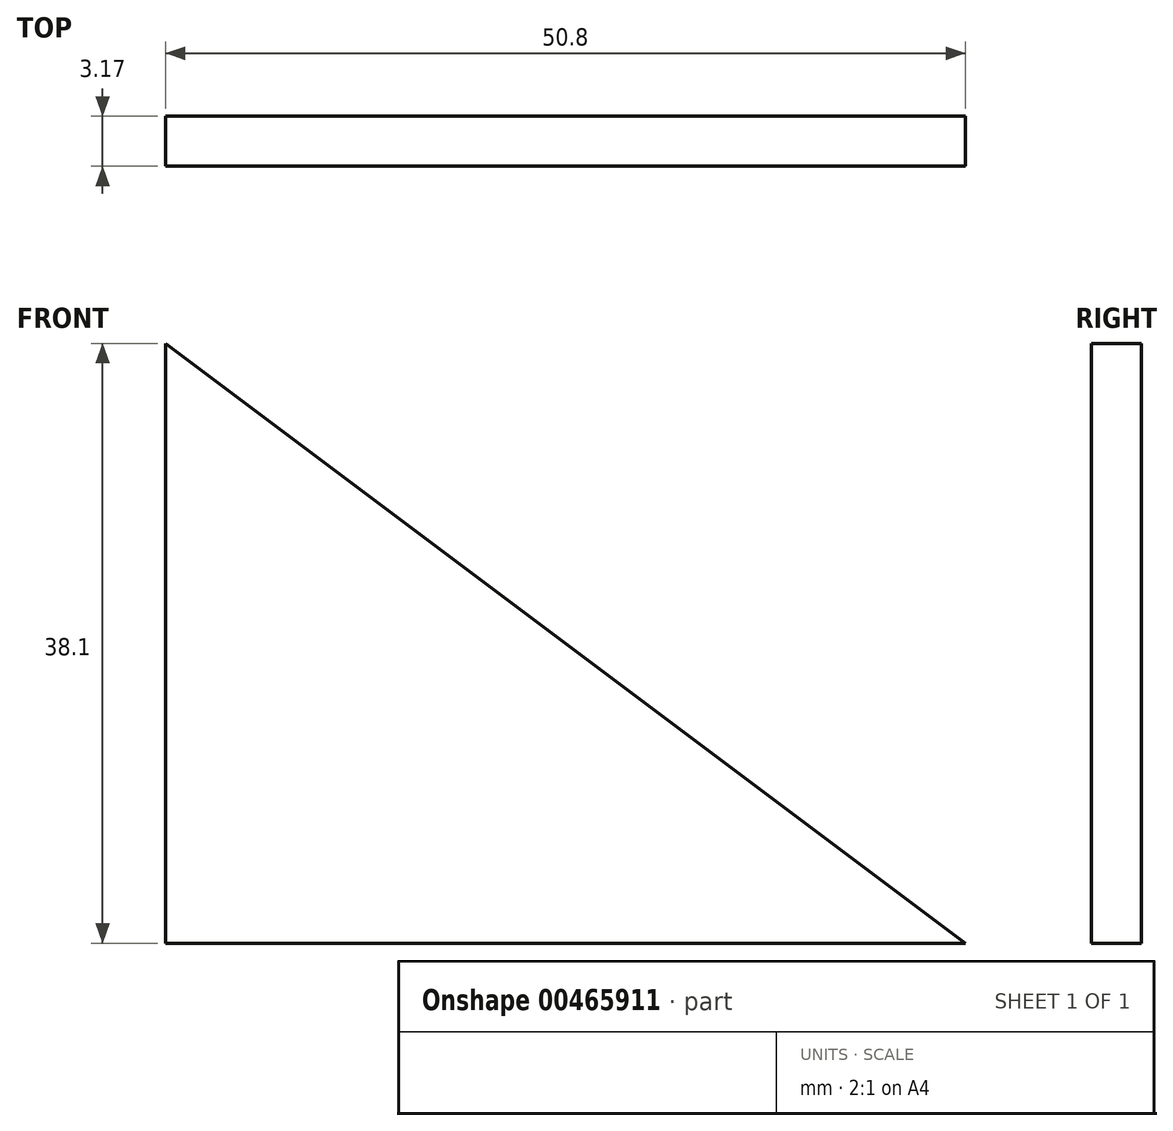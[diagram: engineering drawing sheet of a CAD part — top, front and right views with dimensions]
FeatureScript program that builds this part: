
annotation { "Feature Type Name" : "Feature", "Feature Type Description" : "" }
export const myFeature = defineFeature(function(context is Context, id is Id, definition is map)
    precondition{}
    {
        {
            var Q0;
            Q0=qCreatedBy(makeId("Front.planeOp"),FACE);
            var sketch = newSketch(context, id + "F0", { "sketchPlane" : qUnion([Q0])});
            skLineSegment(sketch, "E0.bottom", {"start": v(-25.4, 19.05) * mm, "end": v(25.4, 19.05) * mm});
            skLineSegment(sketch, "E0.top", {"start": v(-25.4, -19.05) * mm, "end": v(25.4, -19.05) * mm});
            skLineSegment(sketch, "E0.left", {"start": v(-25.4, 19.05) * mm, "end": v(-25.4, -19.05) * mm});
            skLineSegment(sketch, "E0.right", {"start": v(25.4, 19.05) * mm, "end": v(25.4, -19.05) * mm});
            skPoint(sketch, "E0.middle", {"position": v(0, 0) * mm});
            skLineSegment(sketch, "E1", {"start": v(-25.4, 19.05) * mm, "end": v(25.4, -19.05) * mm});
            skSolve(sketch);
        }
        {
            var Q0;
            Q0=makeQuery(id+"F0.imprint","IMPRINT",FACE,{"disambiguationData":[TD([[makeQuery(id+"F0.imprint","IMPRINT",EDGE,{"derivedFrom":sQuery(id+"F0.wireOp",EDGE,"E0.top")}),1.0]])]});
            extrude(context, id + "F1", {"entities" : qUnion([Q0]), "depth" : 3.17 * mm});
        }
    });
